# Revit family: Gira_007030
name_source: partatom
category: Electrical Fixtures
revit_build: Autodesk Revit 2017 (Build: 20160225_1515(x64)
units: mm (PartAtom-declared; Revit-internal decimal feet)

## family parameters
Cut with Voids When Loaded = No
Host = Face
Maintain Annotation Orientation = No
Part Type = Normal
Room Calculation Point = No
Round Connector Dimension = Use Diameter
Shared = No

## types (1)
- Junction box WP SM grey
    BIM = https://media.live.bim.site
    BIMSITE_PRODUCT_ID = 16a34d678cd45cfee8bc65b313821b6171f1db54
    Colour = Sonstige (*de-DE)
    Cost = 0 $
    Default Elevation = 1219 mm
    Description = Junction box WP SM GY Junction box,grey Notes : - The junction box can be equipped with connection adapters for cable ducts or tubes. - With this junction box and the KNX button interface, the water-protected surface-mounted design line can easily be integrated in the KNX system.
    GTIN = 4010337070306
    HAN = 007030
    Halogen free = No
    HeinzeBIM = https://www.heinze.de
    Manufacturer = Gira
    Material = plastic
    URL = https://www.gira.de

## geometry (parser evidence)
native form markers: Blend x2, Sweep x7
no freeform markers — native parametric forms only
